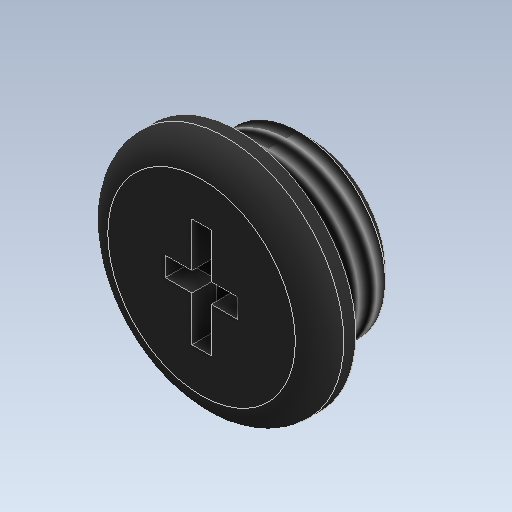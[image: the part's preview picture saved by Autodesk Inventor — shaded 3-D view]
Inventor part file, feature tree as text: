
AUTODESK INVENTOR PART (.ipt)
format: ipt  version: 2021 (Build 250183000, 183)  size: 182,784 bytes
history: native  units: mm
features: extrude x3, sketch x3, fillet x1, thread x1, chamfer x1
ambient origin geometry x8: Origin, YZ Plane, XZ Plane, XY Plane, X Axis, Y Axis, Z Axis, Center Point
bodies: Solid1 (feature_tree)
feature tree (9):
  extrude  "Extrusion1"  Depth=3.0mm TaperAngle=0.0deg
  extrude  "Extrusion2"  Depth=6.0mm
  fillet  "Fillet1"  Radius=6.0mm
  extrude  "Extrusion3"  Depth=9.0mm
  thread  "Thread1"  [1 undecoded]
  chamfer  "Chamfer1"  Distance=1.6mm
  sketch  "Sketch1"  dims[d0=19.5mm d1=3.0mm d2=0.0mm]
  sketch  "Sketch2"  dims[d3=14.4mm d4=2.5mm d5=6.0mm d6=0.0mm]
  sketch  "Sketch3"  dims[d7=2.0mm d8=9.0mm d9=6.0mm d10=1.6mm d11=1.6mm d12=2.0mm d13=0.0mm d14=6.0mm d15=0.0mm d16=1.0mm d17=2.0mm d18=45.0deg]
note: 1 required parameter value undecoded (feature->parameter linkage not recoverable at this tier; creation-order binding heuristic only, values carry confidence <= 0.55)
